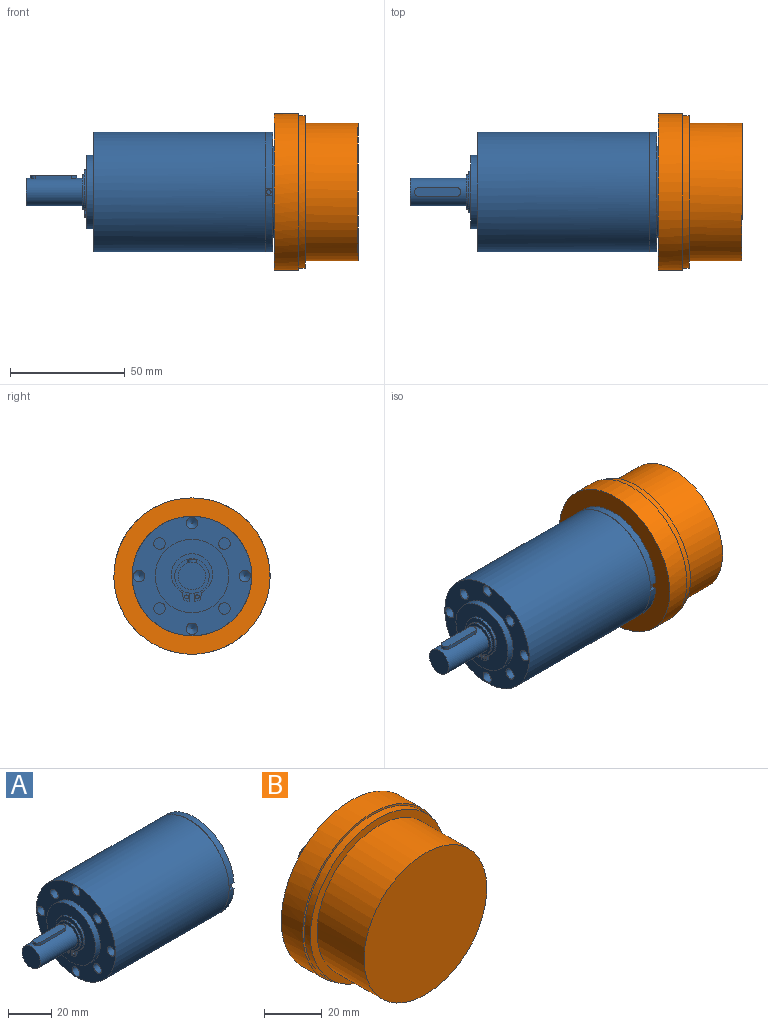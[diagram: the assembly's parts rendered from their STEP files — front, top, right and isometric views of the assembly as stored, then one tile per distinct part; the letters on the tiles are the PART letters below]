
ASSEMBLY  parts=2 mates=1
PART A: 70 faces, bbox 108x52x52 mm
  f0: cylinder r=26mm len=74.6mm, axis (1,0,0), area 12186.9mm2, adj f28,f36
  f1: cylinder r=7.5mm len=15mm, axis (1,0,0), area 42.4mm2, adj f67,f69
  f2: cylinder r=2mm len=4mm, axis (0,0,1), area 9.9mm2, adj f3,f64,f65,f66
  f3: cylinder r=6mm len=24.4mm, axis (1,0,0), area 846.5mm2, adj f2,f4,f64,f65,f68,f69
  f4: cylinder r=2mm len=4mm, axis (0,0,1), area 9.9mm2, adj f3,f64,f65,f66
  f5: cylinder r=7.15mm len=14.3mm, axis (1,0,0), area 47.2mm2, adj f48,f67
  f6: cylinder r=0.85mm len=1.7mm, axis (-1,0,0), area 5.3mm2, adj f61,f63
  f7: cylinder r=0.85mm len=1.7mm, axis (-1,0,0), area 5.3mm2, adj f61,f62
  f8: cylinder r=16mm len=32mm, axis (-1,0,0), area 316.7mm2, adj f28,f48
  f9: cylinder r=1.6mm len=3.9mm, axis (-1,0,0), area 39.2mm2, adj f42,f43
  f10: cylinder r=1.6mm len=3.9mm, axis (-1,0,0), area 39.2mm2, adj f41,f43
  f11: cylinder r=1.6mm len=3.9mm, axis (-1,0,0), area 39.2mm2, adj f40,f43
  f12: cylinder r=11mm len=22mm, axis (1,0,0), area 269.5mm2, adj f39,f43
  f13: cylinder r=25.99mm len=51.98mm, axis (1,0,0), area 528.7mm2, adj f35,f36,f37,f38
  f14: cylinder r=20mm len=40mm, axis (1,0,0), area 75.4mm2, adj f35,f43
  f15: cylinder r=1mm len=5mm, axis (0,1,0), area 31.4mm2, adj f33,f34
  f16: cone r=2.5mm half-angle=59.5deg, axis (-1,0,0), area 22.8mm2, adj f17,f32
  f17: cylinder r=2.5mm len=8mm, axis (-1,0,0), area 125.7mm2, adj f16,f28
  f18: cone r=2.5mm half-angle=59.5deg, axis (-1,0,0), area 22.8mm2, adj f19,f31
  f19: cylinder r=2.5mm len=8mm, axis (-1,0,0), area 125.7mm2, adj f18,f28
  f20: cone r=2.5mm half-angle=59.5deg, axis (-1,0,0), area 22.8mm2, adj f21,f30
  f21: cylinder r=2.5mm len=8mm, axis (-1,0,0), area 125.7mm2, adj f20,f28
  f22: cone r=2.5mm half-angle=59.5deg, axis (-1,0,0), area 22.8mm2, adj f23,f29
  f23: cylinder r=2.5mm len=8mm, axis (-1,0,0), area 125.7mm2, adj f22,f28
  f24: cylinder r=2.5mm len=8mm, axis (-1,0,0), area 125.7mm2, adj f28,f46
  f25: cylinder r=2.5mm len=8mm, axis (-1,0,0), area 125.7mm2, adj f28,f47
  f26: cylinder r=2.5mm len=8mm, axis (-1,0,0), area 125.7mm2, adj f28,f44
  f27: cylinder r=2.5mm len=8mm, axis (-1,0,0), area 125.7mm2, adj f28,f45
  f28: plane 52x52mm, normal (-1,0,0), area 1162.4mm2, adj f0,f8,f17,f19,f21,f23,f24,f25
  f29: plane 0.1x0.1mm, normal (-1,0,0), area 0mm2, adj f22
  f30: plane 0.1x0.1mm, normal (-1,0,0), area 0mm2, adj f20
  f31: plane 0.1x0.1mm, normal (-1,0,0), area 0mm2, adj f18
  f32: plane 0.1x0.1mm, normal (-1,0,0), area 0mm2, adj f16
  f33: plane 3.3x3.1mm, normal (0,-1,0), area 7.1mm2, adj f15,f35,f36,f37,f38
  f34: plane 2x2mm, normal (0,-1,0), area 3.1mm2, adj f15
  f35: plane 51.98x51.93mm, normal (1,0,0), area 859.3mm2, adj f13,f14,f33,f37,f38
  f36: plane 52x52mm, normal (1,0,0), area 7.8mm2, adj f0,f13,f33,f37,f38
  f37: plane 3.3x1.94mm, normal (0,0,1), area 6.4mm2, adj f13,f33,f35,f36
  f38: plane 3.3x1.94mm, normal (0,0,-1), area 6.4mm2, adj f13,f33,f35,f36
  f39: plane 22x22mm, normal (1,0,0), area 380.1mm2, adj f12
  f40: plane 3.2x3.2mm, normal (1,0,0), area 8mm2, adj f11
  f41: plane 3.2x3.2mm, normal (1,0,0), area 8mm2, adj f10
  f42: plane 3.2x3.2mm, normal (1,0,0), area 8mm2, adj f9
  f43: plane 40x40mm, normal (1,0,0), area 852.4mm2, adj f9,f10,f11,f12,f14
  f44: plane 5x5mm, normal (-1,0,0), area 19.6mm2, adj f26
  f45: plane 5x5mm, normal (-1,0,0), area 19.6mm2, adj f27
  f46: plane 5x5mm, normal (-1,0,0), area 19.6mm2, adj f24
  f47: plane 5x5mm, normal (-1,0,0), area 19.6mm2, adj f25
  f48: plane 32x32mm, normal (-1,0,0), area 550.7mm2, adj f5,f8,f49,f50,f51,f52,f53,f54
  f49: cylinder r=9mm len=18mm, axis (-1,0,0), area 46.6mm2, adj f48,f50,f60,f61
  f50: cylinder r=1.5mm len=1.16mm, axis (-1,0,0), area 1.4mm2, adj f48,f49,f51,f61
  f51: plane 1.84x1mm, normal (0,-1,-0.08), area 1.8mm2, adj f48,f50,f52,f61
  f52: cylinder r=1.33mm len=1mm, axis (-1,0,0), area 1mm2, adj f48,f51,f53,f61
  f53: cylinder r=11.3mm len=2.18mm, axis (-1,0,0), area 2.2mm2, adj f48,f52,f54,f61
  f54: plane 3.6x1mm, normal (0,1,0), area 3.6mm2, adj f48,f53,f55,f61
  f55: cylinder r=7.5mm len=15mm, axis (-1,0,0), area 45.1mm2, adj f48,f54,f56,f61
  f56: plane 3.6x1mm, normal (0,-1,0), area 3.6mm2, adj f48,f55,f57,f61
  f57: cylinder r=11.3mm len=2.18mm, axis (-1,0,0), area 2.2mm2, adj f48,f56,f58,f61
  f58: cylinder r=1.33mm len=1mm, axis (-1,0,0), area 1mm2, adj f48,f57,f59,f61
  f59: plane 1.84x1mm, normal (0,1,-0.08), area 1.8mm2, adj f48,f58,f60,f61
  f60: cylinder r=1.5mm len=1.16mm, axis (-1,0,0), area 1.4mm2, adj f48,f49,f59,f61
  f61: plane 20.74x18mm, normal (-1,0,0), area 88.4mm2, adj f6,f7,f49,f50,f51,f52,f53,f54
  f62: plane 1.7x1.7mm, normal (-1,0,0), area 2.3mm2, adj f7
  f63: plane 1.7x1.7mm, normal (-1,0,0), area 2.3mm2, adj f6
  f64: plane 16x1.74mm, normal (0,-1,0), area 27.9mm2, adj f2,f3,f4,f66
  f65: plane 16x1.74mm, normal (0,1,0), area 27.9mm2, adj f2,f3,f4,f66
  f66: plane 20x4mm, normal (0,0,1), area 76.6mm2, adj f2,f4,f64,f65
  f67: plane 15x15mm, normal (1,0,0), area 16.1mm2, adj f1,f5
  f68: plane 12x12mm, normal (-1,0,0), area 113.1mm2, adj f3
  f69: plane 15x15mm, normal (-1,0,0), area 63.6mm2, adj f1,f3
PART B: 12 faces, bbox 68x59.1x68 mm
  f0: cylinder r=30mm len=60mm, axis (0,-1,0), area 4335.4mm2, adj f1,f3
  f1: plane 60x60mm, normal (0,-1,0), area 2827.4mm2, adj f0
  f2: cylinder r=33.2mm len=66.4mm, axis (0,1,0), area 625.8mm2, adj f3,f6
  f3: plane 66.4x66.4mm, normal (0,-1,0), area 635.4mm2, adj f0,f2
  f4: cylinder r=34mm len=68mm, axis (0,1,0), area 2243.1mm2, adj f5,f6
  f5: plane 68x68mm, normal (0,1,0), area 3251.5mm2, adj f4,f7
  f6: plane 68x68mm, normal (0,-1,0), area 168.9mm2, adj f2,f4
  f7: cylinder r=11mm len=22mm, axis (0,-1,0), area 145.1mm2, adj f5,f8
  f8: plane 22x22mm, normal (0,1,0), area 329.9mm2, adj f7,f9
  f9: cylinder r=4mm len=19.5mm, axis (0,-1,0), area 490.1mm2, adj f8,f11
  f10: plane 6x6mm, normal (0,1,0), area 28.3mm2, adj f11
  f11: cone r=3mm half-angle=45deg, axis (0,-1,0), area 31.1mm2, adj f9,f10
PLACE A rot(axis=(0,-1,0),0deg) t=(-31.04,4.26,15.13)mm
PLACE B rot(axis=(0,0,1),90deg) t=(60.96,4.26,15.13)mm
MATE planar A.f43 <-> B.f0  axis (1,0,0) through (47.46,4.29,14.98)mm
